# Revit family: R17-IVLB-Generic-LED Panel
name_source: partatom
category: Lighting Fixtures
revit_build: Autodesk Revit 2017 (Build: 20190508_0315(x64)
units: mm (PartAtom-declared; Revit-internal decimal feet)

## family parameters
Always vertical = Yes
Cut with Voids When Loaded = No
Light Source = Yes
Part Type = Normal
Room Calculation Point = No
Round Connector Dimension = Use Diameter
Shared = No
Work Plane-Based = No

## types (1)
- LED Panel
    Apparent Load = 0 VA
    Assembly Code = 63.0
    Color Filter = 16777215
    Dimming Lamp Color Temperature Shift = <None>
    Emit Shape Visible in Rendering = No
    Emit from Rectangle Length = 1160 mm  [stored 3.80577 ft]
    Emit from Rectangle Width = 260 mm  [stored 0.853018 ft]
    LED Panel = Yes
    LED Panel -  Height = 30 mm  [stored 0.0984252 ft]
    LED Panel - Length = 300 mm
    LED Panel - Width = 1200 mm
    Luminaire Material = Rubber, Silicone
    Manufacturer = LED PANEL
    Model = SPACE RESERVATION
    Photometric Web File = 2x2 2Lamp.ies
    Tilt Angle = 90.00°
    URL = www.ivlibrary.com

note: [stored X ft] marks values corroborated as IEEE doubles in the binary element streams (Revit-internal decimal feet)

## geometry (parser evidence)
native form markers: Sweep x2
no freeform markers — native parametric forms only
